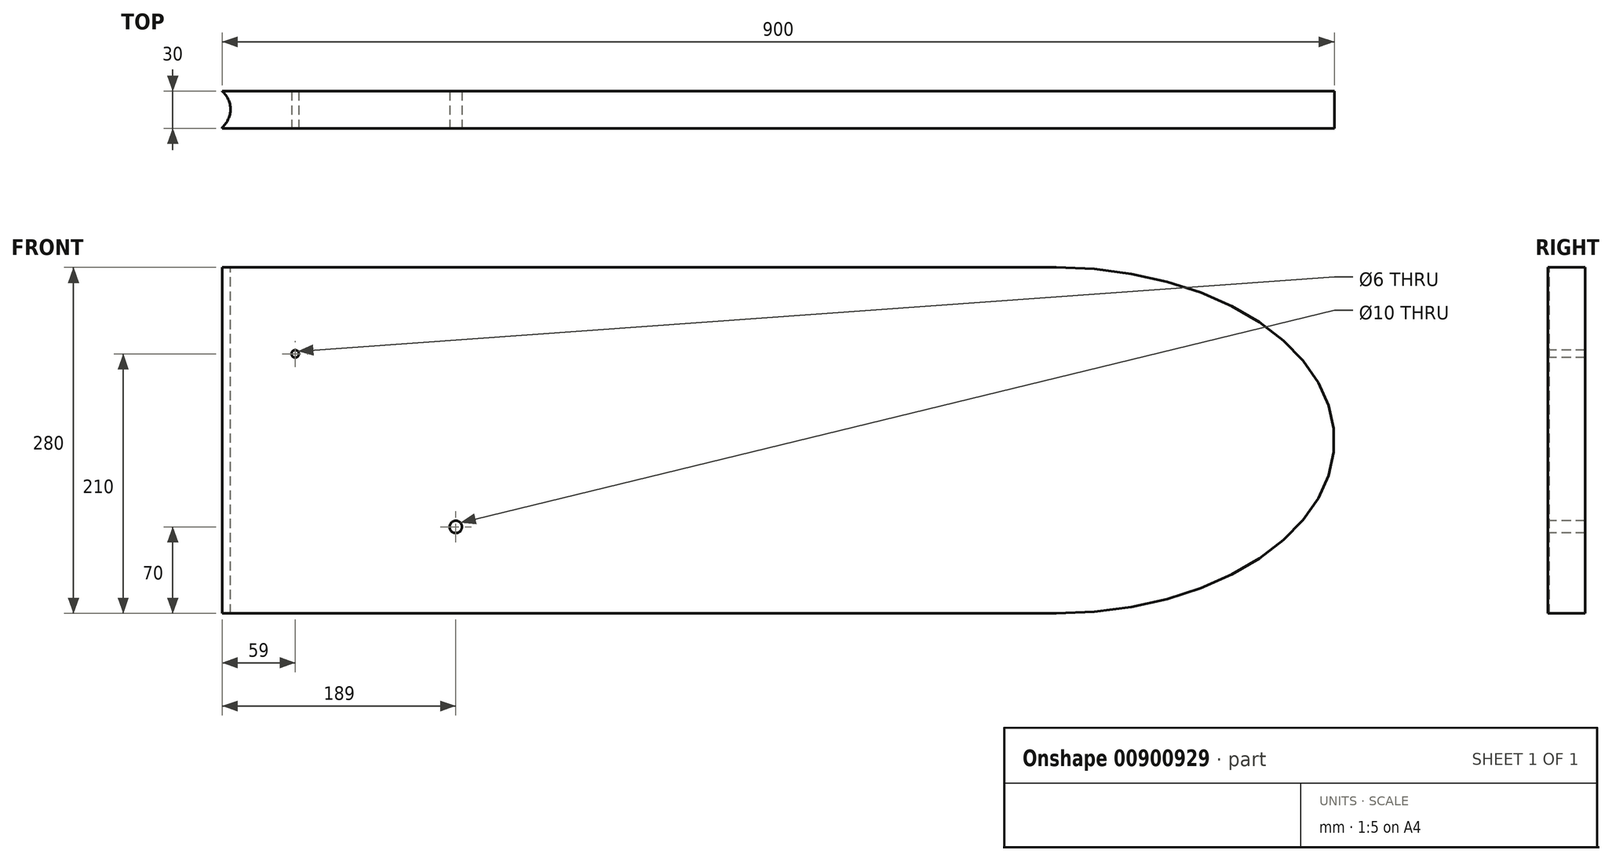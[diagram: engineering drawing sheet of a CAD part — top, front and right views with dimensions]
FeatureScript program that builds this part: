
annotation { "Feature Type Name" : "Feature", "Feature Type Description" : "" }
export const myFeature = defineFeature(function(context is Context, id is Id, definition is map)
    precondition{}
    {
        {
            var Q0;
            Q0=qCreatedBy(makeId("Front.planeOp"),FACE);
            var sketch = newSketch(context, id + "F0", { "sketchPlane" : qUnion([Q0])});
            skLineSegment(sketch, "E0.top", {"start": v(225, -140) * mm, "end": v(-450, -140) * mm});
            skPoint(sketch, "E0.middle", {"position": v(0, 0) * mm});
            skEllipticalArc(sketch, "E1", {});
            skPoint(sketch, "E2.orphan", {"position": v(450, -140) * mm});
            skPoint(sketch, "E0.left.start.orphan", {"position": v(450, 140) * mm});
            skPoint(sketch, "E3.orphan", {"position": v(-487, 140) * mm});
            skLineSegment(sketch, "E4.bottom", {"start": v(225, 140) * mm, "end": v(-450, 140) * mm});
            skLineSegment(sketch, "E4.left", {"start": v(225, 140) * mm, "end": v(225, -140) * mm});
            skLineSegment(sketch, "E4.right", {"start": v(-450, 140) * mm, "end": v(-450, -140) * mm});
            const initialGuessF0  = {"E1": [0.225, 0, 1, 0, 0.225, 0.14, 4.71238898038469, 1.5707963267948966]};
            skSetInitialGuess(sketch, initialGuessF0);
            skSolve(sketch);
        }
        {
            var Q0;
            Q0 = qSketchRegion(id + "F0", true);
            extrude(context, id + "F1", {"entities" : qUnion([Q0]), "endBound" : BoundingType.SYMMETRIC, "depth" : 30 * mm, "offsetDistance" : 25 * mm});
        }
        {
            var Q0;
            Q0=qCreatedBy(makeId("Front.planeOp"),FACE);
            var sketch = newSketch(context, id + "F2", { "sketchPlane" : qUnion([Q0])});
            skCircle(sketch, "E5", {"center": v(-261, -70) * mm, "radius": 5 * mm});
            skCircle(sketch, "E6", {"center": v(-391, 70) * mm, "radius": 3 * mm});
            skSolve(sketch);
        }
        {
            var Q0;
            Q0 = qSketchRegion(id + "F2", true);
            extrude(context, id + "F3", {"entities" : qUnion([Q0]), "operationType" : NewBodyOperationType.REMOVE, "endBound" : BoundingType.SYMMETRIC, "oppositeDirection" : true, "depth" : 30 * mm, "offsetDistance" : 25 * mm});
        }
        {
            var Q0;
            Q0=qCreatedBy(makeId("Top.planeOp"),FACE);
            var sketch = newSketch(context, id + "F4", { "sketchPlane" : qUnion([Q0])});
            skCircle(sketch, "E7", {"center": v(-462.5, 0.42) * mm, "radius": 19.09 * mm});
            skPoint(sketch, "E7.first.point", {"position": v(-450.94, -14.77) * mm});
            skPoint(sketch, "E7.second.point", {"position": v(-450.94, 15.6) * mm});
            skPoint(sketch, "E7.third.point", {"position": v(-479.63, 8.86) * mm});
            skSolve(sketch);
        }
        {
            var Q0;
            Q0 = qSketchRegion(id + "F4", true);
            extrude(context, id + "F5", {"entities" : qUnion([Q0]), "operationType" : NewBodyOperationType.REMOVE, "endBound" : BoundingType.SYMMETRIC, "oppositeDirection" : true, "depth" : 280 * mm, "offsetDistance" : 25 * mm});
        }
    });
